# Revit family: ЗК РАШВОРК арт.102
name_source: partatom
category: Арматура трубопроводов
units: mm (PartAtom-declared; Revit-internal decimal feet)

## family parameters
Всегда вертикально = Да
На основе рабочей плоскости = Нет
Общий = Нет
При загрузке вырезать с полостями = Нет
Размер круглого соединителя = Использовать диаметр
Тип детали = Нормальный

## types (11) — shared parameters
ADSK_Единица измерения = шт
ADSK_Завод-изготовитель = ООО ТД "РАШВОРК"
H2 = 60 мм
URL = https://rwru.ru
Длина = 342 мм
Корпус = GGG40
zero-valued in all types: Отметка по умолчанию

## per-type parameters (varying)
| type | ADSK_Масса | ADSK_Наименование краткое | B | D | D(ISO) | D1 | DN | DN(D) | DNсоединителя | G | H | H1 | H11 | HH | L | L1 | L2 | V1 | f | Высота |
| Задвижка с обрезиненным клином РАШВОРК 102-200-10, DN200, PN10, корпус GGG50, клин - GGG50, уплотнение - EPDM, Ф/Ф, ISO5211, с голым штоком | 55 | 102-200-10 | 20 мм | 340 мм | 175 мм | 110 мм | 200 мм | 30 мм | 200 мм | 266 мм | 469 мм | 408 мм | 320 мм | 22 мм | 230 мм | 150 мм | 100 мм | 310 мм | 3 мм | 115 мм |
| Задвижка с обрезиненным клином РАШВОРК 102-250-10, DN250, PN10, корпус GGG50, клин - GGG50, уплотнение - EPDM, Ф/Ф, ISO5211, с голым штоком | 80 | 102-250-10 | 22 мм | 405 мм | 175 мм | 125 мм | 250 мм | 30 мм | 250 мм | 319 мм | 558 мм | 497 мм | 390 мм | 22 мм | 250 мм | 170 мм | 100 мм | 370 мм | 3 мм | 125 мм |
| Задвижка с обрезиненным клином РАШВОРК 102-300-10, DN300, PN10, корпус GGG50, клин - GGG50, уплотнение - EPDM, Ф/Ф, ISO5211, с голым штоком | 111 | 102-300-10 | 25 мм | 460 мм | 175 мм | 164 мм | 300 мм | 30 мм | 300 мм | 370 мм | 645 мм | 584 мм | 480 мм | 22 мм | 270 мм | 170 мм | 100 мм | 410 мм | 4 мм | 135 мм |
| Задвижка с обрезиненным клином РАШВОРК 102-350-10, DN350, PN10, корпус GGG50, клин - GGG50, уплотнение - EPDM, Ф/Ф, ISO5211, с голым штоком | 228 | 102-350-10 | 27 мм | 520 мм | 175 мм | 198 мм | 350 мм | 36 мм | 350 мм | 429 мм | 830 мм | 775 мм | 645 мм | 22 мм | 290 мм | 210 мм | 100 мм | 530 мм | 4 мм | 145 мм |
| Задвижка с обрезиненным клином РАШВОРК 102-400-10, DN400, PN10, корпус GGG50, клин - GGG50, уплотнение - EPDM, Ф/Ф, ISO5211, с голым штоком | 257 | 102-400-10 | 28 мм | 580 мм | 175 мм | 220 мм | 400 мм | 36 мм | 400 мм | 480 мм | 897 мм | 842 мм | 692 мм | 28 мм | 310 мм | 210 мм | 100 мм | 595 мм | 4 мм | 155 мм |
| Задвижка с обрезиненным клином РАШВОРК 102-500-10, DN500, PN10, корпус GGG50, клин - GGG50, уплотнение - EPDM, Ф/Ф, ISO5211, с голым штоком | 387 | 102-500-10 | 32 мм | 715 мм | 210 мм | 275 мм | 500 мм | 40 мм | 500 мм | 582 мм | 1084 мм | 1024 мм | 920 мм | 26 мм | 350 мм | 284 мм | 130 мм | 700 мм | 4 мм | 175 мм |
| Задвижка с обрезиненным клином РАШВОРК 102-600-10, DN600, PN10, корпус GGG50, клин - GGG50, уплотнение - EPDM, Ф/Ф, ISO5211, с голым штоком | 484 | 102-600-10 | 36 мм | 780 мм | 210 мм | 300 мм | 600 мм | 40 мм | 600 мм | 682 мм | 1237 мм | 1177 мм | 1035 мм | 26 мм | 390 мм | 312 мм | 130 мм | 775 мм | 5 мм | 195 мм |
| Задвижка с обрезиненным клином РАШВОРК 102-700-10, DN700, PN10, корпус GGG50, клин - GGG50, уплотнение - EPDM, Ф/Ф, ISO5211, с голым штоком | 820.4 | 102-700-10 | 40 мм | 910 мм | 300 мм | 380 мм | 700 мм | 60 мм | 700 мм | 794 мм | 1532 мм | 1468 мм | 1290 мм | 25 мм | 430 мм | 312 мм | 200 мм | 970 мм | 5 мм | 215 мм |
| Задвижка с обрезиненным клином РАШВОРК 102-800-10, DN800, PN10, корпус GGG50, клин - GGG50, уплотнение - EPDM, Ф/Ф, ISO5211, с голым штоком | 1130.4 | 102-800-10 | 43 мм | 1025 мм | 300 мм | 430 мм | 800 мм | 65 мм | 800 мм | 901 мм | 1705 мм | 1640 мм | 1470 мм | 25 мм | 470 мм | 330 мм | 200 мм | 1050 мм | 5 мм | 235 мм |
| Задвижка с обрезиненным клином РАШВОРК 102-900-10, DN900, PN10, корпус GGG50, клин - GGG50, уплотнение - EPDM, Ф/Ф, ISO5211, с голым штоком | 1580.4 | 102-900-10 | 47 мм | 1125 мм | 300 мм | 460 мм | 900 мм | 70 мм | 900 мм | 1005 мм | 1800 мм | 1735 мм | 1580 мм | 25 мм | 510 мм | 360 мм | 200 мм | 1100 мм | 5 мм | 255 мм |
| Задвижка с обрезиненным клином РАШВОРК 102-1000-10, DN1000, PN10, корпус GGG50, клин - GGG50, уплотнение - EPDM, Ф/Ф, ISO5211, с голым штоком | 2980.4 | 102-1000-10 | 50 мм | 1255 мм | 300 мм | 500 мм | 1000 мм | 75 мм | 1000 мм | 1112 мм | 1918 мм | 1853 мм | 1700 мм | 25 мм | 550 мм | 382 мм | 200 мм | 1260 мм | 5 мм | 275 мм |

note: column(s) folded — value = type name in every type: ADSK_Наименование

## geometry (parser evidence)
native form markers: Blend x4
no freeform markers — native parametric forms only
